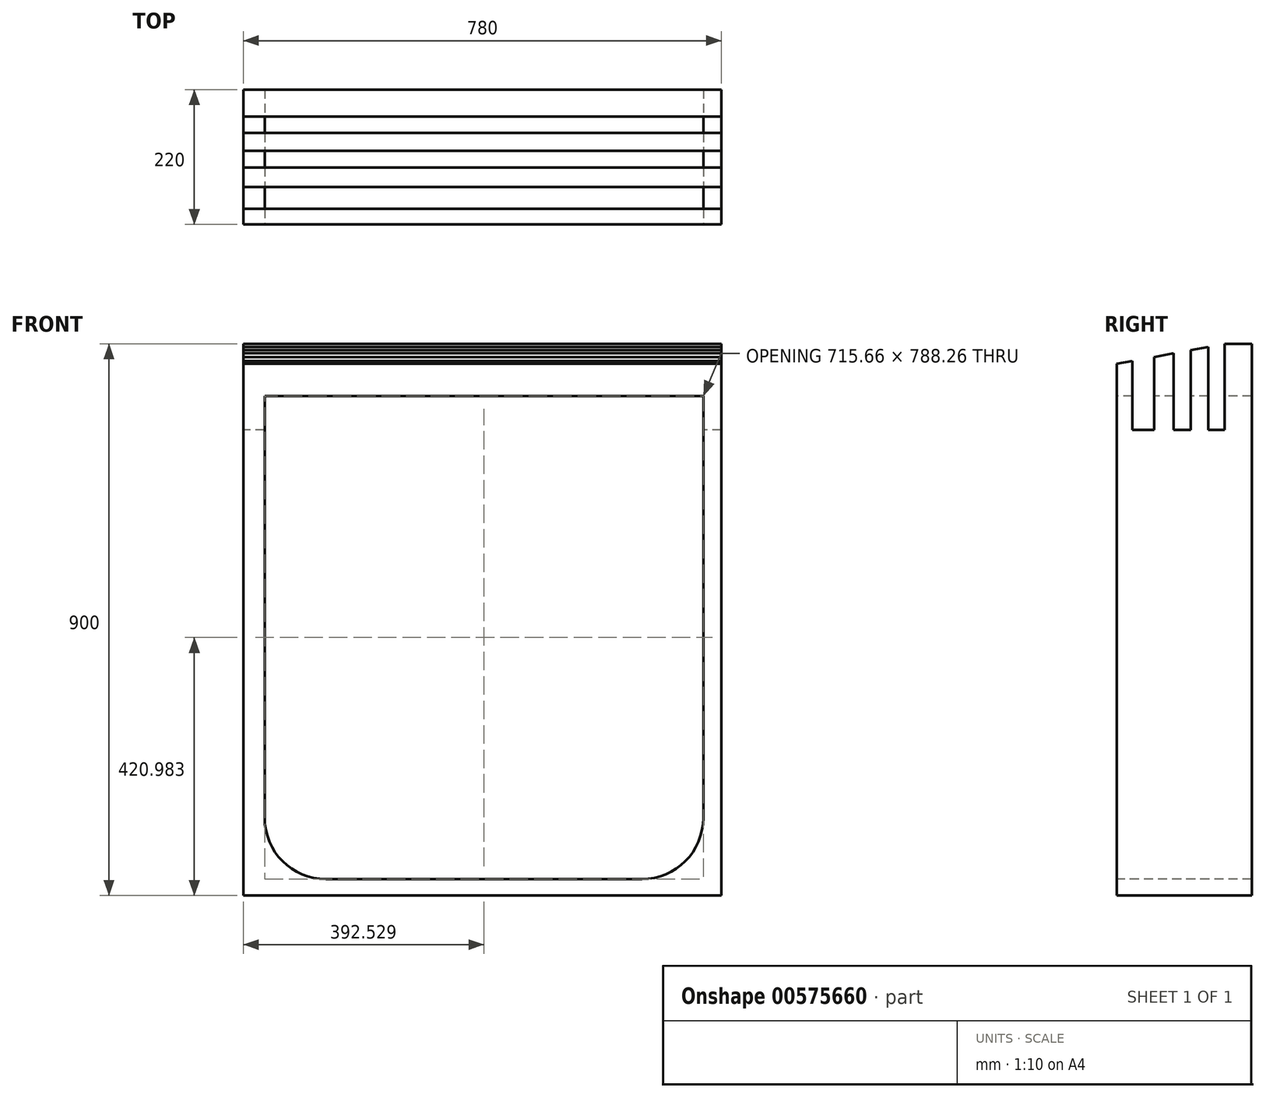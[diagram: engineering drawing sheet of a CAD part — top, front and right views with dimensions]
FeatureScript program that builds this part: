
annotation { "Feature Type Name" : "Feature", "Feature Type Description" : "" }
export const myFeature = defineFeature(function(context is Context, id is Id, definition is map)
    precondition{}
    {
        {
            var Q0;
            Q0=qCreatedBy(makeId("Top.planeOp"),FACE);
            var sketch = newSketch(context, id + "F0", { "sketchPlane" : qUnion([Q0])});
            skLineSegment(sketch, "E0.bottom", {"start": v(0, 0) * mm, "end": v(-780, 0) * mm});
            skLineSegment(sketch, "E0.top", {"start": v(0, 220) * mm, "end": v(-780, 220) * mm});
            skLineSegment(sketch, "E0.left", {"start": v(0, 0) * mm, "end": v(0, 220) * mm});
            skLineSegment(sketch, "E0.right", {"start": v(-780, 0) * mm, "end": v(-780, 220) * mm});
            skSolve(sketch);
        }
        {
            var Q0;
            Q0 = qSketchRegion(id + "F0", true);
            extrude(context, id + "F1", {"entities" : qUnion([Q0]), "depth" : 900 * mm, "offsetDistance" : 25 * mm});
        }
        {
            var Q0;
            Q0=makeQuery(id+"F1.opExtrude","SWEPT_FACE",FACE,{"disambiguationData":[OSD([sQuery(id+"F0.wireOp",EDGE,"E0.bottom")])]});
            var sketch = newSketch(context, id + "F2", { "sketchPlane" : qUnion([Q0])});
            skLineSegment(sketch, "E1.bottom", {"start": v(-29.64, 26.85) * mm, "end": v(-745.3, 26.85) * mm});
            skLineSegment(sketch, "E1.top", {"start": v(-29.64, 815.12) * mm, "end": v(-745.3, 815.12) * mm});
            skLineSegment(sketch, "E1.left", {"start": v(-29.64, 26.85) * mm, "end": v(-29.64, 815.12) * mm});
            skLineSegment(sketch, "E1.right", {"start": v(-745.3, 26.85) * mm, "end": v(-745.3, 815.12) * mm});
            skSolve(sketch);
        }
        {
            var Q0;
            Q0 = qSketchRegion(id + "F2", true);
            extrude(context, id + "F3", {"entities" : qUnion([Q0]), "operationType" : NewBodyOperationType.REMOVE, "endBound" : BoundingType.UP_TO_NEXT, "oppositeDirection" : true, "depth" : 25 * mm, "offsetDistance" : 25 * mm});
        }
        {
            var Q0;
            Q0=makeQuery(id+"F1.opExtrude","SWEPT_FACE",FACE,{"disambiguationData":[OSD([sQuery(id+"F0.wireOp",EDGE,"E0.left")])]});
            var sketch = newSketch(context, id + "F4", { "sketchPlane" : qUnion([Q0])});
            skLineSegment(sketch, "E2", {"start": v(175.82, 900) * mm, "end": v(0, 867.35) * mm});
            skLineSegment(sketch, "E3", {"start": v(0, 867.35) * mm, "end": v(0, 900) * mm});
            skLineSegment(sketch, "E4", {"start": v(0, 900) * mm, "end": v(175.82, 900) * mm});
            skSolve(sketch);
        }
        {
            var Q0;
            Q0 = qSketchRegion(id + "F4", true);
            extrude(context, id + "F5", {"entities" : qUnion([Q0]), "operationType" : NewBodyOperationType.REMOVE, "endBound" : BoundingType.UP_TO_NEXT, "oppositeDirection" : true, "depth" : 25 * mm, "offsetDistance" : 25 * mm});
        }
        {
            var Q0;
            Q0=makeQuery(id+"F1.opExtrude","CAP_FACE",FACE,{"disambiguationData":[OSD([sQuery(id+"F0.wireOp",EDGE,"E0.bottom"),sQuery(id+"F0.wireOp",EDGE,"E0.top"),sQuery(id+"F0.wireOp",EDGE,"E0.left"),sQuery(id+"F0.wireOp",EDGE,"E0.right")])],"isStart":false});
            var sketch = newSketch(context, id + "F6", { "sketchPlane" : qUnion([Q0])});
            skLineSegment(sketch, "E5.bottom", {"start": v(0, 120.31) * mm, "end": v(-780, 120.31) * mm});
            skLineSegment(sketch, "E5.top", {"start": v(0, 92.82) * mm, "end": v(-780, 92.82) * mm});
            skLineSegment(sketch, "E5.left", {"start": v(0, 120.31) * mm, "end": v(0, 92.82) * mm});
            skLineSegment(sketch, "E5.right", {"start": v(-780, 120.31) * mm, "end": v(-780, 92.82) * mm});
            skLineSegment(sketch, "E6.bottom", {"start": v(-780, 60.72) * mm, "end": v(0, 60.72) * mm});
            skLineSegment(sketch, "E6.top", {"start": v(-780, 25.35) * mm, "end": v(0, 25.35) * mm});
            skLineSegment(sketch, "E6.left", {"start": v(-780, 60.72) * mm, "end": v(-780, 25.35) * mm});
            skLineSegment(sketch, "E6.right", {"start": v(0, 60.72) * mm, "end": v(0, 25.35) * mm});
            skLineSegment(sketch, "E7.bottom", {"start": v(-780, 175.82) * mm, "end": v(0, 175.82) * mm});
            skLineSegment(sketch, "E7.top", {"start": v(-780, 149.22) * mm, "end": v(0, 149.22) * mm});
            skLineSegment(sketch, "E7.left", {"start": v(-780, 175.82) * mm, "end": v(-780, 149.22) * mm});
            skLineSegment(sketch, "E7.right", {"start": v(0, 175.82) * mm, "end": v(0, 149.22) * mm});
            skSolve(sketch);
        }
        {
            var Q0;
            Q0 = qSketchRegion(id + "F6", true);
            extrude(context, id + "F7", {"entities" : qUnion([Q0]), "operationType" : NewBodyOperationType.REMOVE, "oppositeDirection" : true, "depth" : 140 * mm, "offsetDistance" : 25 * mm});
        }
        {
            var Q0;
            Q0=makeQuery(id+"F3.boolean.opBoolean","COPY",EDGE,{"derivedFrom":makeQuery(id+"F3.opExtrude","SWEPT_EDGE",EDGE,{"disambiguationData":[OSD([sQuery(id+"F2.wireOp",EDGE,"E1.bottom"),sQuery(id+"F2.wireOp",EDGE,"E1.right")])]})});
            var Q1;
            Q1=makeQuery(id+"F3.boolean.opBoolean","COPY",EDGE,{"derivedFrom":makeQuery(id+"F3.opExtrude","SWEPT_EDGE",EDGE,{"disambiguationData":[OSD([sQuery(id+"F2.wireOp",EDGE,"E1.bottom"),sQuery(id+"F2.wireOp",EDGE,"E1.left")])]})});
            fillet(context, id + "F8", {"entities" : qUnion([Q0, Q1]), "radius" : 100 * mm, "tangentPropagation" : true, "allowEdgeOverflow" : false});
        }
    });
